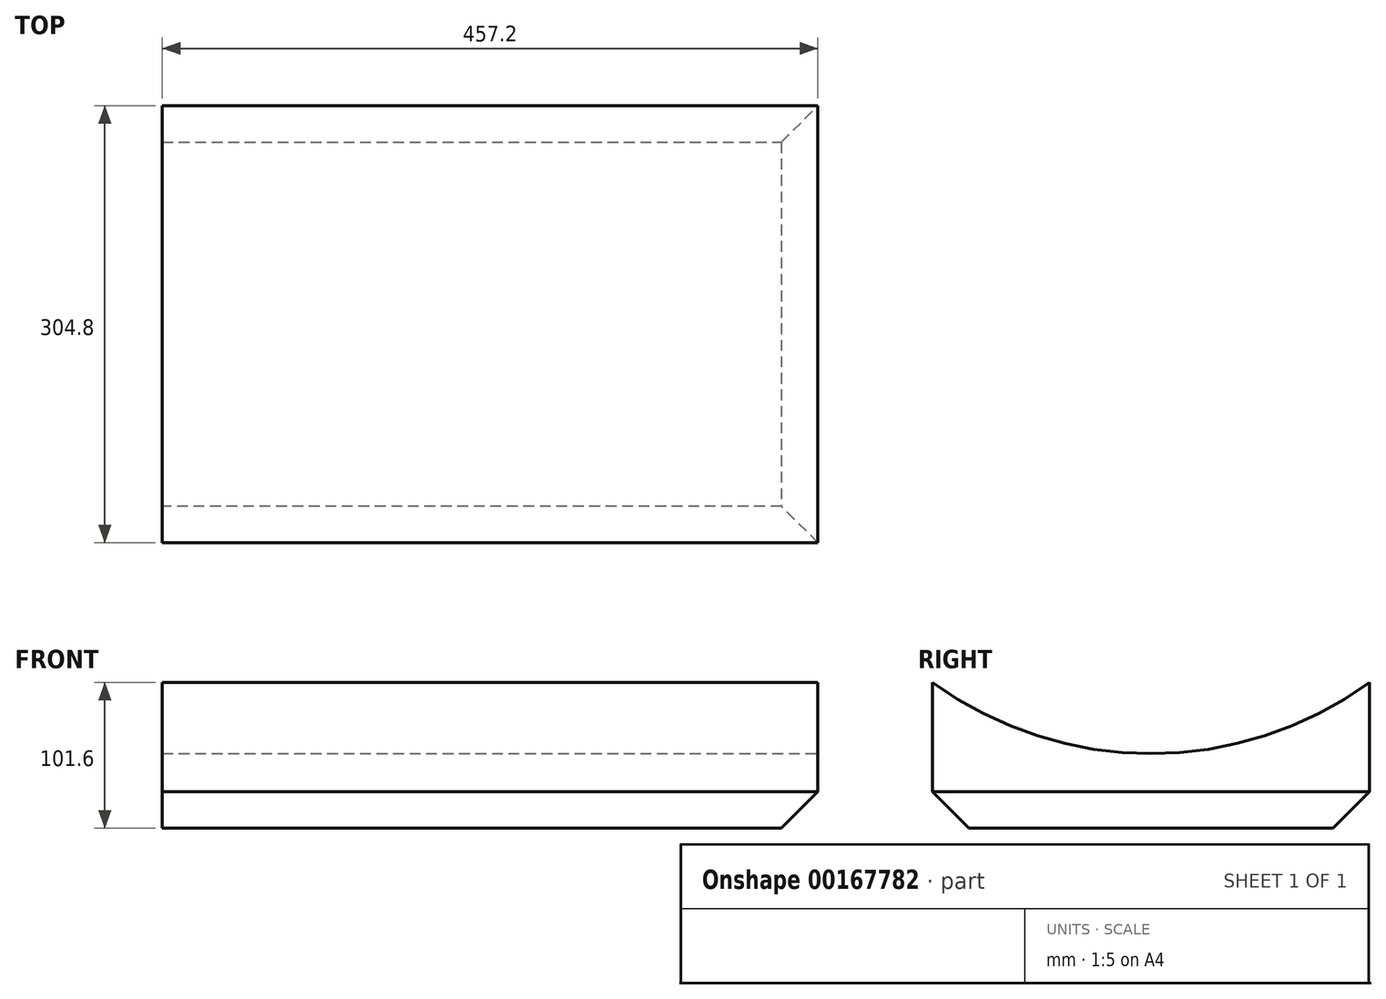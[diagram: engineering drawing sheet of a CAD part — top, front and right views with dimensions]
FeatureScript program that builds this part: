
annotation { "Feature Type Name" : "Feature", "Feature Type Description" : "" }
export const myFeature = defineFeature(function(context is Context, id is Id, definition is map)
    precondition{}
    {
        {
            var Q0;
            Q0=qCreatedBy(makeId("Top.planeOp"),FACE);
            var sketch = newSketch(context, id + "F0", { "sketchPlane" : qUnion([Q0])});
            skLineSegment(sketch, "E0.bottom", {"start": v(-228.6, 152.4) * mm, "end": v(228.6, 152.4) * mm});
            skLineSegment(sketch, "E0.top", {"start": v(-228.6, -152.4) * mm, "end": v(228.6, -152.4) * mm});
            skLineSegment(sketch, "E0.left", {"start": v(-228.6, 152.4) * mm, "end": v(-228.6, -152.4) * mm});
            skLineSegment(sketch, "E0.right", {"start": v(228.6, 152.4) * mm, "end": v(228.6, -152.4) * mm});
            skPoint(sketch, "E0.middle", {"position": v(0, 0) * mm});
            skSolve(sketch);
        }
        {
            var Q0;
            Q0 = qSketchRegion(id + "F0", true);
            extrude(context, id + "F1", {"entities" : qUnion([Q0]), "endBound" : BoundingType.SYMMETRIC, "depth" : 101.6 * mm});
        }
        {
            var Q0;
            Q0=makeQuery(id+"F1.opExtrude","SWEPT_FACE",FACE,{"disambiguationData":[OSD([sQuery(id+"F0.wireOp",EDGE,"E0.right")])]});
            var sketch = newSketch(context, id + "F2", { "sketchPlane" : qUnion([Q0])});
            skCircle(sketch, "E1", {"center": v(0, 260.04) * mm, "radius": 258.86 * mm});
            skSolve(sketch);
        }
        {
            var Q0;
            Q0 = qSketchRegion(id + "F2", true);
            var Q1;
            Q1=makeQuery(id+"F1.opExtrude","SWEPT_FACE",FACE,{"disambiguationData":[OSD([sQuery(id+"F0.wireOp",EDGE,"E0.left")])]});
            extrude(context, id + "F3", {"entities" : qUnion([Q0]), "operationType" : NewBodyOperationType.REMOVE, "endBound" : BoundingType.UP_TO_SURFACE, "oppositeDirection" : true, "endBoundEntityFace" : qUnion([Q1]), "depth" : 25.4 * mm});
        }
        {
            var Q0;
            Q0=makeQuery(id+"F1.opExtrude","CAP_EDGE",EDGE,{"disambiguationData":[OSD([sQuery(id+"F0.wireOp",EDGE,"E0.top")])],"isStart":true});
            chamfer(context, id + "F4", {"entities" : qUnion([Q0]), "width" : 25.4 * mm, "tangentPropagation" : true});
        }
        {
            var Q0;
            Q0=makeQuery(id+"F1.opExtrude","CAP_EDGE",EDGE,{"disambiguationData":[OSD([sQuery(id+"F0.wireOp",EDGE,"E0.right")])],"isStart":true});
            var Q1;
            Q1=makeQuery(id+"F1.opExtrude","CAP_EDGE",EDGE,{"disambiguationData":[OSD([sQuery(id+"F0.wireOp",EDGE,"E0.bottom")])],"isStart":true});
            chamfer(context, id + "F5", {"entities" : qUnion([Q0, Q1]), "width" : 25.4 * mm, "tangentPropagation" : true});
        }
    });
